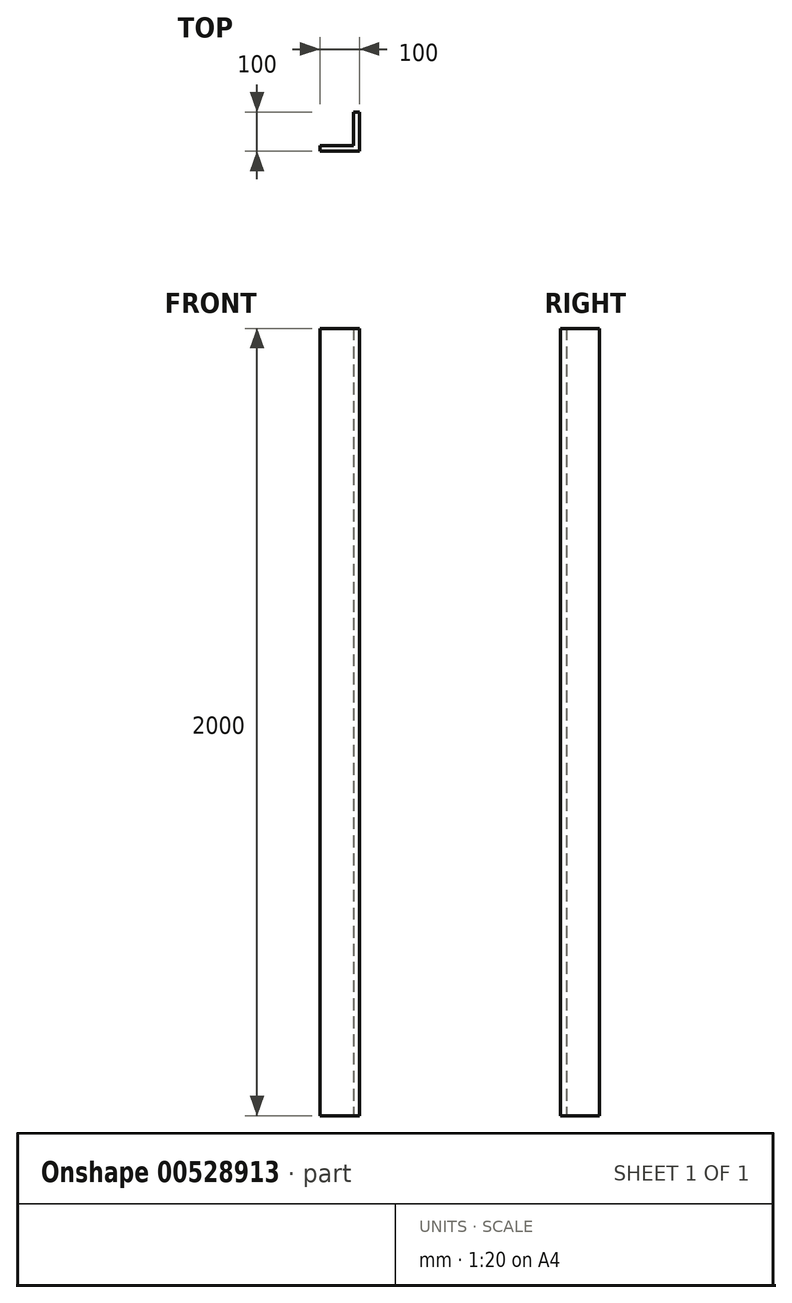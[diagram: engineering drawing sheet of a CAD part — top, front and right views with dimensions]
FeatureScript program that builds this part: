
annotation { "Feature Type Name" : "Feature", "Feature Type Description" : "" }
export const myFeature = defineFeature(function(context is Context, id is Id, definition is map)
    precondition{}
    {
        {
            var Q0;
            Q0=qCreatedBy(makeId("Top.planeOp"),FACE);
            var sketch = newSketch(context, id + "F0", { "sketchPlane" : qUnion([Q0])});
            skLineSegment(sketch, "E0", {"start": v(0, 0) * mm, "end": v(0, 100) * mm});
            skLineSegment(sketch, "E1", {"start": v(0, 100) * mm, "end": v(-15, 100) * mm});
            skLineSegment(sketch, "E2", {"start": v(-100, 15) * mm, "end": v(-100, 0) * mm});
            skLineSegment(sketch, "E3", {"start": v(-100, 0) * mm, "end": v(0, 0) * mm});
            skLineSegment(sketch, "E4", {"start": v(-15, 100) * mm, "end": v(-15, 15) * mm});
            skLineSegment(sketch, "E5", {"start": v(-15, 15) * mm, "end": v(-100, 15) * mm});
            skSolve(sketch);
        }
        {
            var Q0;
            Q0 = qSketchRegion(id + "F0", true);
            extrude(context, id + "F1", {"entities" : qUnion([Q0]), "depth" : 2000 * mm, "offsetDistance" : 25 * mm});
        }
    });
